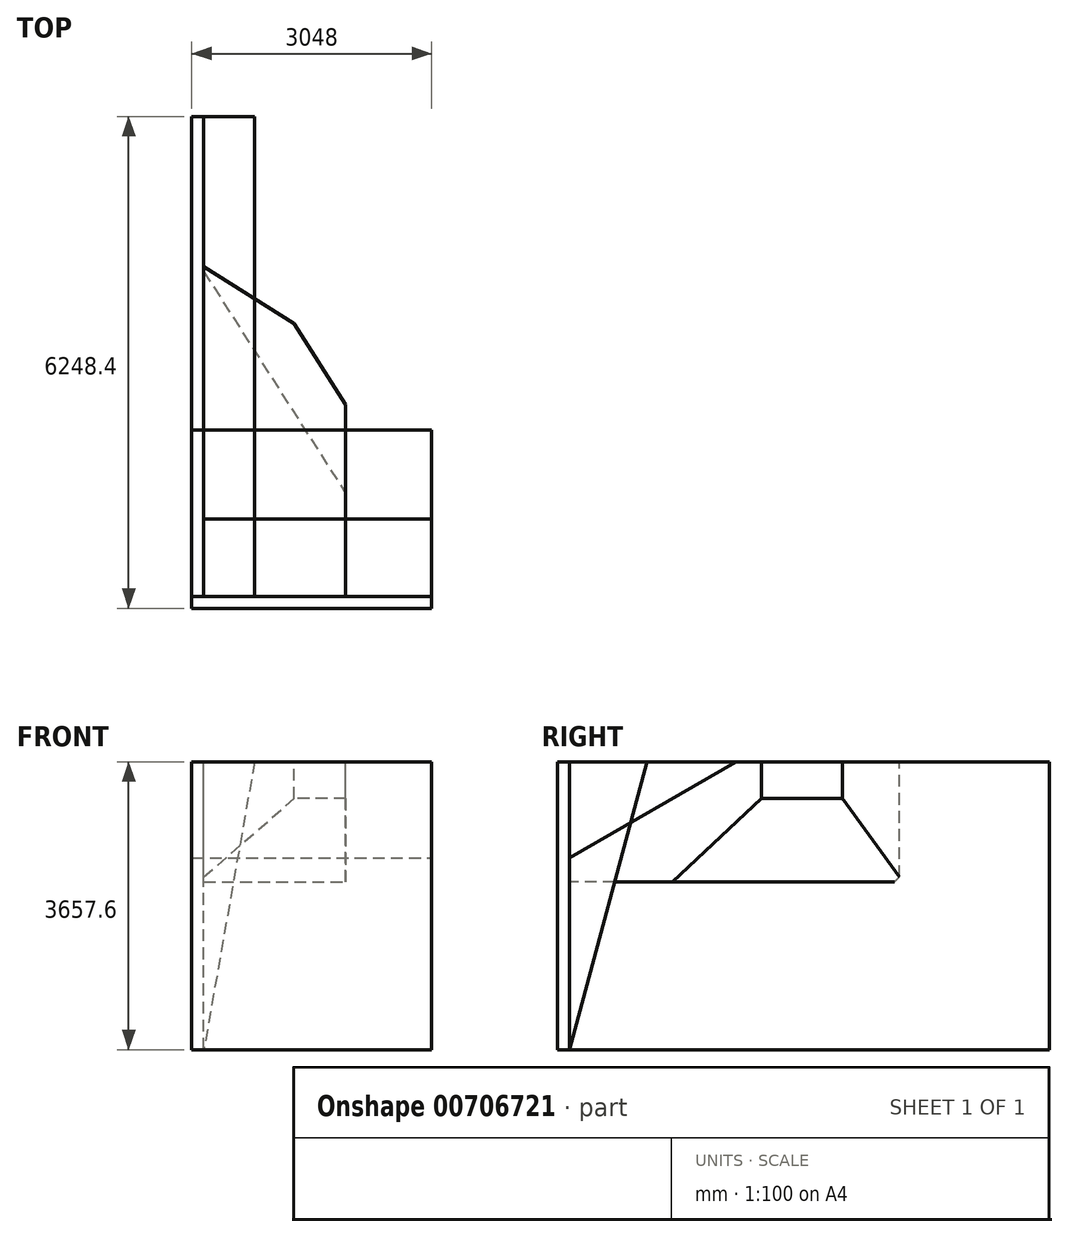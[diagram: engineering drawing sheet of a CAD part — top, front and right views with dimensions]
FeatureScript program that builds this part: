
annotation { "Feature Type Name" : "Feature", "Feature Type Description" : "" }
export const myFeature = defineFeature(function(context is Context, id is Id, definition is map)
    precondition{}
    {
        {
            var Q0;
            Q0=qCreatedBy(makeId("Front.planeOp"),FACE);
            var sketch = newSketch(context, id + "F0", { "sketchPlane" : qUnion([Q0])});
            skLineSegment(sketch, "E0.bottom", {"start": v(0, 0) * mm, "end": v(3048, 0) * mm});
            skLineSegment(sketch, "E0.top", {"start": v(0, 3657.6) * mm, "end": v(3048, 3657.6) * mm});
            skLineSegment(sketch, "E0.left", {"start": v(0, 0) * mm, "end": v(0, 3657.6) * mm});
            skLineSegment(sketch, "E0.right", {"start": v(3048, 0) * mm, "end": v(3048, 3657.6) * mm});
            skSolve(sketch);
        }
        {
            var Q0;
            Q0=makeQuery(id+"F0.imprint","IMPRINT",FACE,{"disambiguationData":[TD([[makeQuery(id+"F0.imprint","IMPRINT",EDGE,{"derivedFrom":sQuery(id+"F0.wireOp",EDGE,"E0.bottom")}),1.0]])]});
            extrude(context, id + "F1", {"entities" : qUnion([Q0]), "depth" : 152.4 * mm, "offsetDistance" : 25.4 * mm});
        }
        {
            var Q0;
            Q0=qCreatedBy(makeId("Right.planeOp"),FACE);
            var sketch = newSketch(context, id + "F2", { "sketchPlane" : qUnion([Q0])});
            skLineSegment(sketch, "E1.bottom", {"start": v(0, 0) * mm, "end": v(6096, 0) * mm});
            skLineSegment(sketch, "E1.top", {"start": v(0, 3657.6) * mm, "end": v(6096, 3657.6) * mm});
            skLineSegment(sketch, "E1.left", {"start": v(0, 0) * mm, "end": v(0, 3657.6) * mm});
            skLineSegment(sketch, "E1.right", {"start": v(6096, 0) * mm, "end": v(6096, 3657.6) * mm});
            skSolve(sketch);
        }
        {
            var Q0;
            Q0=makeQuery(id+"F2.imprint","IMPRINT",FACE,{"disambiguationData":[TD([[makeQuery(id+"F2.imprint","IMPRINT",EDGE,{"derivedFrom":sQuery(id+"F2.wireOp",EDGE,"E1.bottom")}),1.0]])]});
            extrude(context, id + "F3", {"entities" : qUnion([Q0]), "operationType" : NewBodyOperationType.ADD, "depth" : 152.4 * mm, "offsetDistance" : 25.4 * mm});
        }
        {
            var Q0;
            Q0=makeQuery(id+"F1.opExtrude","SWEPT_FACE",FACE,{"disambiguationData":[OSD([sQuery(id+"F0.wireOp",EDGE,"E0.right")])]});
            var sketch = newSketch(context, id + "F4", { "sketchPlane" : qUnion([Q0])});
            skLineSegment(sketch, "E2", {"start": v(0, 0) * mm, "end": v(0, 3657.6) * mm});
            skLineSegment(sketch, "E3", {"start": v(0, 3657.6) * mm, "end": v(980.05, 3657.6) * mm});
            skLineSegment(sketch, "E4", {"start": v(980.05, 3657.6) * mm, "end": v(0, 0) * mm});
            skSolve(sketch);
        }
        {
            var Q0;
            Q0 = qSketchRegion(id + "F4", true);
            extrude(context, id + "F5", {"entities" : qUnion([Q0]), "endBound" : BoundingType.UP_TO_NEXT, "oppositeDirection" : true, "depth" : 25.4 * mm, "offsetDistance" : 25.4 * mm});
        }
        {
            var Q0;
            Q0=makeQuery(id+"F3.boolean.opBoolean","MERGE",FACE,{"derivedFrom":[makeQuery(id+"F1.opExtrude","SWEPT_FACE",FACE,{"disambiguationData":[OSD([sQuery(id+"F0.wireOp",EDGE,"E0.top")])]}),makeQuery(id+"F3.opExtrude","SWEPT_FACE",FACE,{"disambiguationData":[OSD([sQuery(id+"F2.wireOp",EDGE,"E1.top")])]})]});
            var sketch = newSketch(context, id + "F6", { "sketchPlane" : qUnion([Q0])});
            skLineSegment(sketch, "E5", {"start": v(1297.8, 3465.74) * mm, "end": v(1954.32, 2438.4) * mm});
            skLineSegment(sketch, "E6", {"start": v(1954.32, 2438.4) * mm, "end": v(1954.32, 0) * mm});
            skLineSegment(sketch, "E7", {"start": v(1954.32, 0) * mm, "end": v(152.4, 0) * mm});
            skLineSegment(sketch, "E8", {"start": v(1297.8, 3465.74) * mm, "end": v(152.4, 4188.82) * mm});
            skLineSegment(sketch, "E9", {"start": v(152.4, 4188.82) * mm, "end": v(152.4, 0) * mm});
            skSolve(sketch);
        }
        {
            var Q0;
            Q0 = qSketchRegion(id + "F6", true);
            extrude(context, id + "F7", {"entities" : qUnion([Q0]), "oppositeDirection" : true, "depth" : 1524 * mm, "offsetDistance" : 25.4 * mm});
        }
        {
            var Q0;
            Q0=makeQuery(id+"F7.opExtrude","CAP_EDGE",EDGE,{"disambiguationData":[OSD([sQuery(id+"F6.wireOp",EDGE,"E5")])],"isStart":false});
            chamfer(context, id + "F8", {"entities" : qUnion([Q0]), "chamferType" : ChamferType.OFFSET_ANGLE, "width" : 609.6 * mm, "oppositeDirection" : false, "angle" : 60 * degree});
        }
        {
            var Q0;
            Q0=makeQuery(id+"F3.opExtrude","SWEPT_FACE",FACE,{"disambiguationData":[OSD([sQuery(id+"F2.wireOp",EDGE,"E1.right")])]});
            var sketch = newSketch(context, id + "F9", { "sketchPlane" : qUnion([Q0])});
            skLineSegment(sketch, "E10", {"start": v(-152.4, 0) * mm, "end": v(-152.4, 3657.6) * mm});
            skLineSegment(sketch, "E11", {"start": v(-152.4, 3657.6) * mm, "end": v(-797.33, 3657.6) * mm});
            skLineSegment(sketch, "E12", {"start": v(-797.33, 3657.6) * mm, "end": v(-152.4, 0) * mm});
            skSolve(sketch);
        }
        {
            var Q0;
            Q0=makeQuery(id+"F9.imprint","IMPRINT",FACE,{"disambiguationData":[TD([[makeQuery(id+"F9.imprint","IMPRINT",EDGE,{"derivedFrom":sQuery(id+"F9.wireOp",EDGE,"E10")}),1.0]])]});
            var Q1;
            Q1=makeQuery(id+"F7.opExtrude","SWEPT_FACE",FACE,{"disambiguationData":[OSD([sQuery(id+"F6.wireOp",EDGE,"NLeem1OF-F4fu-5Kkd-w4ls-eyMZTuJwcAZx")])]});
            extrude(context, id + "F10", {"entities" : qUnion([Q0]), "oppositeDirection" : true, "depth" : 20 * 304.8 * mm, "endBoundEntityFace" : qUnion([Q1]), "offsetDistance" : 25.4 * mm});
        }
        {
            var Q0;
            Q0=makeQuery(id+"F1.opExtrude","SWEPT_FACE",FACE,{"disambiguationData":[OSD([sQuery(id+"F0.wireOp",EDGE,"E0.right")])]});
            var sketch = newSketch(context, id + "F11", { "sketchPlane" : qUnion([Q0])});
            skLineSegment(sketch, "E13", {"start": v(0, 3657.6) * mm, "end": v(2111.72, 3657.6) * mm});
            skLineSegment(sketch, "E14", {"start": v(2111.72, 3657.6) * mm, "end": v(0, 2438.4) * mm});
            skLineSegment(sketch, "E15", {"start": v(0, 2438.4) * mm, "end": v(0, 3657.6) * mm});
            skSolve(sketch);
        }
        {
            var Q0;
            Q0=makeQuery(id+"F11.imprint","IMPRINT",FACE,{"disambiguationData":[TD([[makeQuery(id+"F11.imprint","IMPRINT",EDGE,{"derivedFrom":sQuery(id+"F11.wireOp",EDGE,"E13")}),-1.0]])]});
            extrude(context, id + "F12", {"entities" : qUnion([Q0]), "oppositeDirection" : true, "depth" : 12 * 254 * mm, "offsetDistance" : 25.4 * mm});
        }
    });
